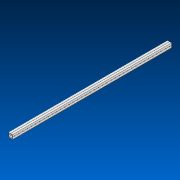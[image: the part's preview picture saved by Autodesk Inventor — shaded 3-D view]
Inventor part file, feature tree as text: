
AUTODESK INVENTOR PART (.ipt)
format: ipt  version: 2022.2 (Build 262287000, 287)  size: 805,376 bytes
history: native  units: in
note: dims shown in document units (in); Inventor stores cm internally (conversion verified against a paired STEP export)
features: other x38, extrude x1, pattern_linear x1, sketch x1, pattern_circular x1
ambient origin geometry x8: Origin, YZ Plane, XZ Plane, XY Plane, X Axis, Y Axis, Z Axis, Center Point
bodies: Solid1 (feature_tree)
feature tree (42):
  extrude  "Extrusion1"  Depth=1.0in
  other  "Work Axis1"
  pattern_linear  "Rectangular Pattern1"  Spacing1=0.0in  [1 undecoded]
  sketch  "Sketch1"  dims[d0=1.0in d1=21.0in d2=0.0in d3=14.9606in d5=1.0in]
  other  "Work Axis2"
  other  "Work Axis3"
  other  "Work Axis4"
  other  "Work Axis5"
  other  "Work Axis6"
  other  "Work Axis7"
  other  "Work Axis8"
  other  "Work Axis9"
  other  "Work Axis10"
  other  "Work Axis11"
  other  "Work Axis12"
  other  "Work Axis13"
  other  "Work Axis14"
  other  "Work Axis15"
  other  "Work Axis16"
  other  "Work Axis17"
  other  "Work Axis18"
  other  "Work Axis19"
  other  "Work Axis20"
  other  "Work Axis21"
  other  "Work Axis22"
  other  "Work Axis23"
  other  "Work Axis24"
  other  "Work Axis25"
  other  "Work Axis26"
  other  "Work Axis27"
  other  "Work Axis28"
  other  "Work Axis29"
  other  "Work Axis30"
  other  "Work Axis31"
  other  "Work Axis32"
  other  "Work Axis33"
  other  "Work Axis34"
  other  "Work Axis35"
  other  "Work Axis36"
  other  "Work Axis37"
  other  "Work Axis40"
  pattern_circular  "CirPattern2"
note: 1 required parameter value undecoded (feature->parameter linkage not recoverable at this tier; creation-order binding heuristic only, values carry confidence <= 0.55)
